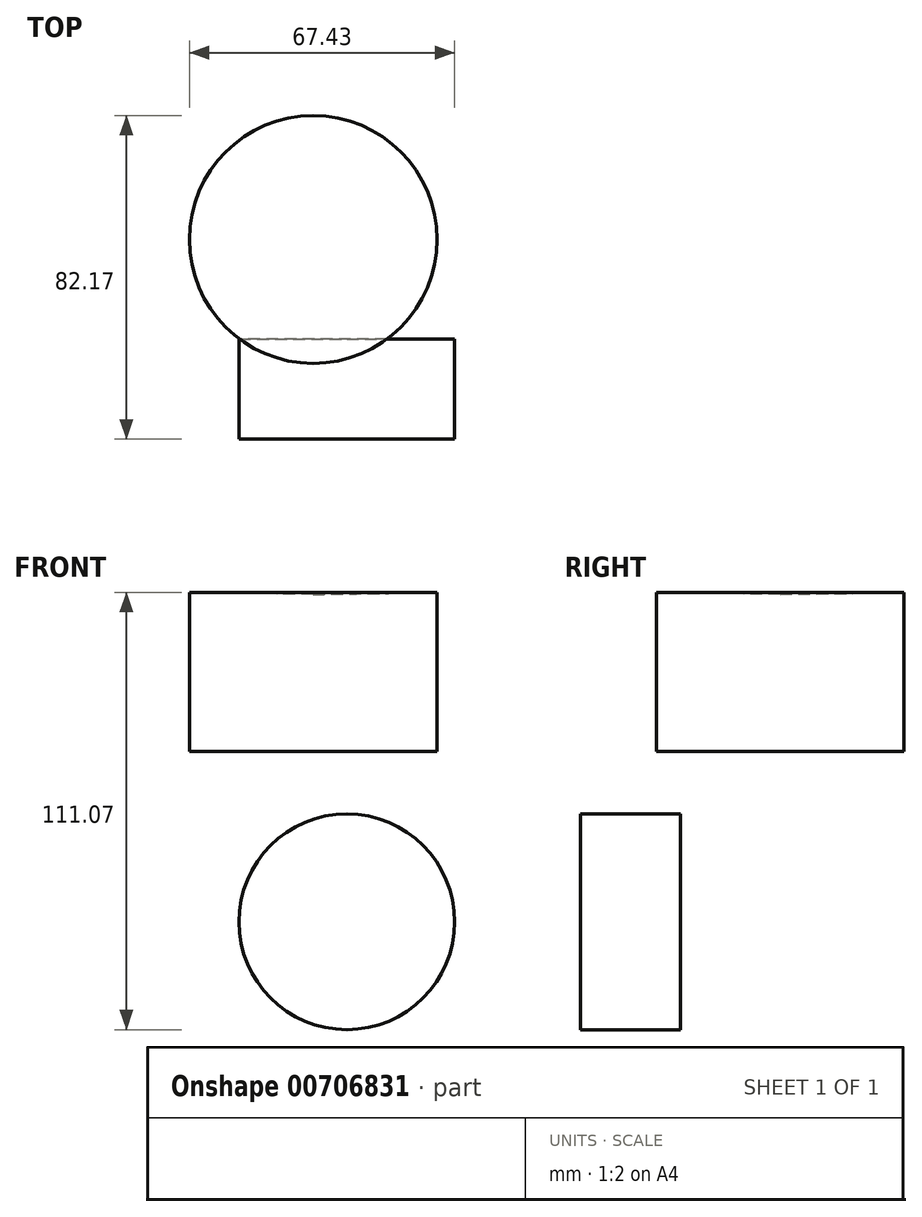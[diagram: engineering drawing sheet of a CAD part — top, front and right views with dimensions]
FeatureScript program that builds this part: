
annotation { "Feature Type Name" : "Feature", "Feature Type Description" : "" }
export const myFeature = defineFeature(function(context is Context, id is Id, definition is map)
    precondition{}
    {
        {
            var Q0;
            Q0=qCreatedBy(makeId("Front.planeOp"),FACE);
            var sketch = newSketch(context, id + "F0", { "sketchPlane" : qUnion([Q0])});
            skLineSegment(sketch, "E0", {"start": v(97.21, 106.44) * mm, "end": v(79.46, 114.3) * mm});
            skLineSegment(sketch, "E1", {"start": v(78.16, 109.6) * mm, "end": v(79.46, 97.85) * mm});
            skLineSegment(sketch, "E2", {"start": v(78.16, 109.6) * mm, "end": v(79.46, 114.3) * mm});
            skLineSegment(sketch, "E3", {"start": v(78.16, 109.6) * mm, "end": v(79.46, 118.45) * mm});
            skLineSegment(sketch, "E4", {"start": v(79.46, 97.85) * mm, "end": v(65.17, 92.43) * mm});
            skLineSegment(sketch, "E5", {"start": v(65.17, 92.43) * mm, "end": v(74.26, 82.5) * mm});
            skLineSegment(sketch, "E6", {"start": v(69.72, 87.46) * mm, "end": v(60.4, 69.4) * mm});
            skCircle(sketch, "E7", {"center": v(8.55, -26.04) * mm, "radius": 27.41 * mm});
            skPoint(sketch, "E7.first.point", {"position": v(0, 0) * mm});
            skPoint(sketch, "E7.second.point", {"position": v(17.1, 0) * mm});
            skPoint(sketch, "E7.third.point", {"position": v(-18.84, -24.92) * mm});
            skSolve(sketch);
        }
        {
            var Q0;
            Q0 = qSketchRegion(id + "F0", true);
            extrude(context, id + "F1", {"entities" : qUnion([Q0]), "depth" : 25.4 * mm, "offsetDistance" : 25.4 * mm});
        }
        {
            var Q0;
            Q0=qCreatedBy(makeId("Right.planeOp"),FACE);
            var sketch = newSketch(context, id + "F2", { "sketchPlane" : qUnion([Q0])});
            skLineSegment(sketch, "E8", {"start": v(56.77, 57.62) * mm, "end": v(56.77, 17.19) * mm});
            skLineSegment(sketch, "E9", {"start": v(56.77, 17.19) * mm, "end": v(25.3, 17.19) * mm});
            skLineSegment(sketch, "E10", {"start": v(25.3, 17.19) * mm, "end": v(25.3, 57.13) * mm});
            skLineSegment(sketch, "E11", {"start": v(25.3, 57.13) * mm, "end": v(56.77, 57.62) * mm});
            skSolve(sketch);
        }
        {
            var Q0;
            Q0=makeQuery(id+"F2.imprint","IMPRINT",FACE,{"disambiguationData":[TD([[makeQuery(id+"F2.imprint","IMPRINT",EDGE,{"derivedFrom":sQuery(id+"F2.wireOp",EDGE,"E8")}),-1.0]])]});
            var Q1;
            Q1=sQuery(id+"F2.wireOp",EDGE,"E10");
            revolve(context, id + "F3", {"surfaceOperationType" : NewSurfaceOperationType.NEW, "entities" : qUnion([Q0]), "axis" : qUnion([Q1]), "revolveType" : RevolveType.FULL});
        }
    });
